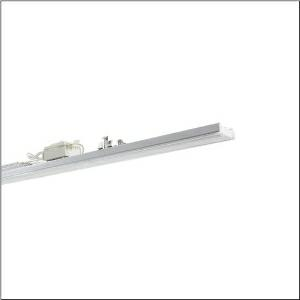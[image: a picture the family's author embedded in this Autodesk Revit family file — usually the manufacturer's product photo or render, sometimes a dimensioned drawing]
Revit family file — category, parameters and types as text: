
# Revit family: licross_11_recessed_ho_51tl12dv4m2m
name_source: partatom
category: Lighting Fixtures
units: mm (PartAtom-declared; Revit-internal decimal feet)

## family parameters
Cut with Voids When Loaded = No
Host = Face
Light Source = No
Part Type = Normal
Room Calculation Point = No
Round Connector Dimension = Use Diameter
Shared = No

## types (1)
- --- (1 x LED, 27150 lm, 150.5 W, 4000K)
    Apparent Load = 150 VA
    CIE Flux Codes = 66 91 98 100 100
    Color Rendering = 80
    Color Temperature = 4000K
    Default Elevation = 1800 mm
    Description = Licross 11 Recessed HO, luminaire insert, of sheet steel, coil coated, white, length: 2.250mm, width: 66mm, height: 67mm, LED rated luminous flux: 27.150lm, light colour: 840, SDCM (Standard Deviation of Colour Matching)MacAdam ≤ 2 SDCM (initial), control gear: DALI 2, with plug, 5-pole, with phase selection, mains connection: 220..240V, AC, 50/60Hz, rated input power: 151W, internal wiring halogen-free, primary optical cover: cover, of PMMA, light emission: direct distribution, primary light characteristic: symmetric, protection rating (complete): IP40, insulation class (complete): insulation class I (protective earthing), certification: CE, ENEC, VDE, UKCA, protection symbol: D if used in an environment without relevant dust loads with corresponding accessories, impact resistance: IK06, permissible ambient temperature for indoor applications: -40..+35°C, corresponds to IFS (International Featured Standards) requirements for safety and quality in the food industry, reducing of maximum allowable ambient temperature of 5°C with ceiling mounting, LABS conformity tested according to VDMA 24364:2018-05, The light source and the operating device comply with the requirements of the Ecodesign Regulation (EU) 2019/2020 and are replaceable in accordance with this regulation, packaging unit: 1 piece
    Height = 58 mm
    Lamp = 1 x LED
    Lamp Light Flux = 27150 lm
    Lamp Power = 150.5 W
    Lamp count = 1
    Length = 2250 mm
    Luminous efficacy = 180 lm/W
    Manufacturer = Siteco
    ModVariant = No
    Model = 51TL12DV4M2M
    Mounting Place = Ceiling
    Mounting Type = Pendant
    Number of Poles = 1
    OnlyDefault = Yes
    Power Factor = 1
    Product Name = Licross 11 Recessed HO
    Product group = luminaire insert | ceiling pendant
    ProductGroupID = 901
    Protection Class = Protection class I
    Protection Degree = IP 40
    RLX_Detail_Level = 1
    RLX_Emergency_Light_Flux = 0 lm
    RLX_Emergency_Type = 0
    RLX_Emergency_Type_DB = No
    RlxData = <blob elided: 29777 chars, md5=68cd588a>
    Socket = socket
    Standby Power = 0 W
    System Light Flux = 27150 lm
    System Power = 150 W
    Type Comments = factory setting: luminous flux: 100 % | dim-lin: 254 | 690 mA
    Type Image = l_1296930.jpg
    URL = http://relux.com
    VarID = @adj_101231
    Voltage = 0 V
    Weight = 0.00 kg
    Width = 66 mm

## geometry (parser evidence)
native form markers: Blend x4, Sweep x11
no freeform markers — native parametric forms only
